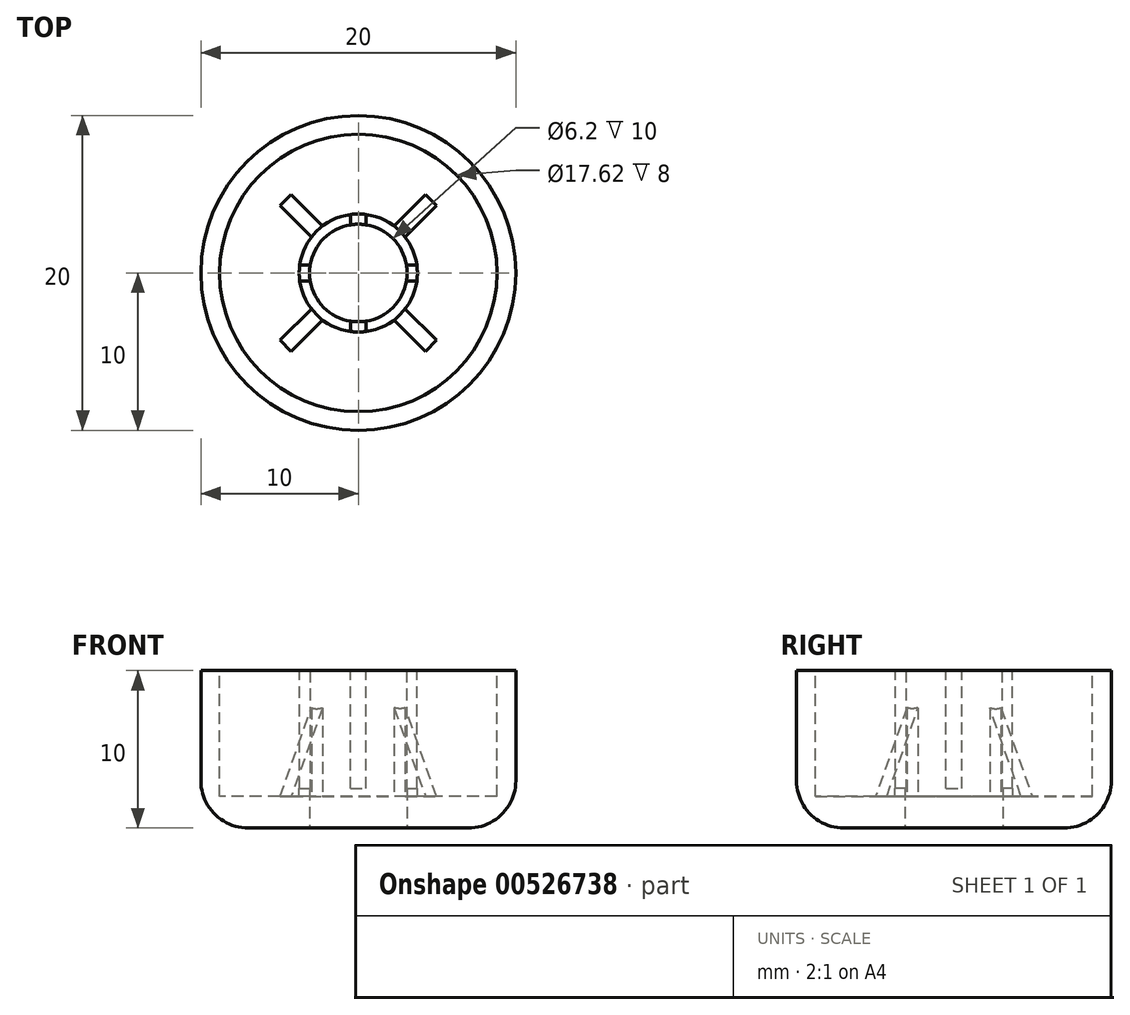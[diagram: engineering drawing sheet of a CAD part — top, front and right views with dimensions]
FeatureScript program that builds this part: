
annotation { "Feature Type Name" : "Feature", "Feature Type Description" : "" }
export const myFeature = defineFeature(function(context is Context, id is Id, definition is map)
    precondition{}
    {
        {
            var Q0;
            Q0=qCreatedBy(makeId("Top.planeOp"),FACE);
            var sketch = newSketch(context, id + "F0", { "sketchPlane" : qUnion([Q0])});
            skCircle(sketch, "E0", {"center": v(0, 0) * mm, "radius": 3.1 * mm});
            skCircle(sketch, "E1", {"center": v(0, 0) * mm, "radius": 10 * mm});
            skSolve(sketch);
        }
        {
            var Q0;
            Q0 = qSketchRegion(id + "F0", true);
            extrude(context, id + "F1", {"entities" : qUnion([Q0]), "depth" : 10 * mm, "offsetDistance" : 25.4 * mm});
        }
        {
            var Q0;
            Q0=makeQuery(id+"F1.opExtrude","CAP_FACE",FACE,{"disambiguationData":[OSD([sQuery(id+"F0.wireOp",EDGE,"E0"),sQuery(id+"F0.wireOp",EDGE,"E1")])],"isStart":false});
            var sketch = newSketch(context, id + "F2", { "sketchPlane" : qUnion([Q0])});
            skCircle(sketch, "E2", {"center": v(0, 0) * mm, "radius": 3.75 * mm});
            skCircle(sketch, "E3", {"center": v(0, 0) * mm, "radius": 8.8 * mm});
            skSolve(sketch);
        }
        {
            var Q0;
            Q0 = qSketchRegion(id + "F2", true);
            extrude(context, id + "F3", {"entities" : qUnion([Q0]), "operationType" : NewBodyOperationType.REMOVE, "oppositeDirection" : true, "depth" : 8 * mm, "offsetDistance" : 25.4 * mm});
        }
        {
            var Q0;
            {var subQ0=sQuery(id+"F0.wireOp",EDGE,"E0");Q0=makeQuery(id+"F3.boolean.opBoolean","SPLIT",FACE,{"disambiguationData":[TD([makeQuery(id+"F1.opExtrude","SWEPT_FACE",FACE,{"disambiguationData":[OSD([subQ0])]})])],"derivedFrom":makeQuery(id+"F1.opExtrude","CAP_FACE",FACE,{"disambiguationData":[OSD([subQ0,sQuery(id+"F0.wireOp",EDGE,"E1")])],"isStart":false})});}
            var sketch = newSketch(context, id + "F4", { "sketchPlane" : qUnion([Q0])});
            skLineSegment(sketch, "E4", {"start": v(-4.82, 0.5) * mm, "end": v(-2.74, 0.5) * mm});
            skLineSegment(sketch, "E5", {"start": v(-2.74, 0.5) * mm, "end": v(-2.74, -0.5) * mm});
            skLineSegment(sketch, "E6", {"start": v(-2.74, -0.5) * mm, "end": v(-4.86, -0.5) * mm});
            skLineSegment(sketch, "E7", {"start": v(-4.86, -0.5) * mm, "end": v(-4.82, 0.5) * mm});
            skPoint(sketch, "E8.start.orphan", {"position": v(0.06, 5.71) * mm});
            skPoint(sketch, "E9.start.orphan", {"position": v(0.06, -3.27) * mm});
            skLineSegment(sketch, "E10", {"start": v(-0.5, 4.69) * mm, "end": v(-0.5, 1.98) * mm});
            skLineSegment(sketch, "E11", {"start": v(-0.5, 1.98) * mm, "end": v(0.5, 1.98) * mm});
            skLineSegment(sketch, "E12", {"start": v(0.5, 1.98) * mm, "end": v(0.5, 4.89) * mm});
            skLineSegment(sketch, "E13", {"start": v(0.5, 4.89) * mm, "end": v(-0.5, 4.89) * mm});
            skLineSegment(sketch, "E14", {"start": v(-0.5, 4.89) * mm, "end": v(-0.5, 4.69) * mm});
            skLineSegment(sketch, "E15.bottom", {"start": v(-0.5, -1.61) * mm, "end": v(0.5, -1.61) * mm});
            skLineSegment(sketch, "E15.top", {"start": v(-0.5, -4.9) * mm, "end": v(0.5, -4.9) * mm});
            skLineSegment(sketch, "E15.left", {"start": v(-0.5, -1.61) * mm, "end": v(-0.5, -4.9) * mm});
            skLineSegment(sketch, "E15.right", {"start": v(0.5, -1.61) * mm, "end": v(0.5, -4.9) * mm});
            skLineSegment(sketch, "E16.bottom", {"start": v(2.33, 0.5) * mm, "end": v(4.84, 0.5) * mm});
            skLineSegment(sketch, "E16.top", {"start": v(2.33, -0.5) * mm, "end": v(4.84, -0.5) * mm});
            skLineSegment(sketch, "E16.left", {"start": v(2.33, 0.5) * mm, "end": v(2.33, -0.5) * mm});
            skLineSegment(sketch, "E16.right", {"start": v(4.84, 0.5) * mm, "end": v(4.84, -0.5) * mm});
            skSolve(sketch);
        }
        {
            var Q0;
            Q0 = qSketchRegion(id + "F4", true);
            extrude(context, id + "F5", {"entities" : qUnion([Q0]), "operationType" : NewBodyOperationType.REMOVE, "oppositeDirection" : true, "depth" : 7.5 * mm, "offsetDistance" : 25.4 * mm});
        }
        {
            var Q0;
            Q0=makeQuery(id+"F1.opExtrude","CAP_EDGE",EDGE,{"disambiguationData":[OSD([sQuery(id+"F0.wireOp",EDGE,"E1")])],"isStart":true});
            fillet(context, id + "F6", {"entities" : qUnion([Q0]), "radius" : 3 * mm, "tangentPropagation" : true, "allowEdgeOverflow" : false});
        }
        {
            var Q0;
            Q0=makeQuery(id+"F3.boolean.opBoolean","COPY",FACE,{"derivedFrom":makeQuery(id+"F3.opExtrude","CAP_FACE",FACE,{"disambiguationData":[OSD([sQuery(id+"F2.wireOp",EDGE,"E2"),sQuery(id+"F2.wireOp",EDGE,"E3")])],"isStart":false})});
            var sketch = newSketch(context, id + "F7", { "sketchPlane" : qUnion([Q0])});
            skLineSegment(sketch, "E17", {"start": v(-2.98, 2.27) * mm, "end": v(-4.98, 4.27) * mm});
            skLineSegment(sketch, "E18", {"start": v(-4.98, 4.27) * mm, "end": v(-4.27, 4.98) * mm});
            skLineSegment(sketch, "E19", {"start": v(-4.27, 4.98) * mm, "end": v(-2.27, 2.98) * mm});
            skLineSegment(sketch, "E20", {"start": v(-2.27, 2.98) * mm, "end": v(-2.98, 2.27) * mm});
            skLineSegment(sketch, "E21.MirrorCS", {"start": v(2.98, 2.27) * mm, "end": v(4.98, 4.27) * mm});
            skLineSegment(sketch, "E22.MirrorCS", {"start": v(4.98, 4.27) * mm, "end": v(4.27, 4.98) * mm});
            skLineSegment(sketch, "E23.MirrorCS", {"start": v(4.27, 4.98) * mm, "end": v(2.27, 2.98) * mm});
            skLineSegment(sketch, "E24.MirrorCS", {"start": v(2.27, 2.98) * mm, "end": v(2.98, 2.27) * mm});
            skLineSegment(sketch, "E25.MirrorCS", {"start": v(-2.98, -2.27) * mm, "end": v(-4.98, -4.27) * mm});
            skLineSegment(sketch, "E26.MirrorCS", {"start": v(-4.98, -4.27) * mm, "end": v(-4.27, -4.98) * mm});
            skLineSegment(sketch, "E27.MirrorCS", {"start": v(-4.27, -4.98) * mm, "end": v(-2.27, -2.98) * mm});
            skLineSegment(sketch, "E28.MirrorCS", {"start": v(2.27, -2.98) * mm, "end": v(2.98, -2.27) * mm});
            skLineSegment(sketch, "E29.MirrorCS", {"start": v(-2.27, -2.98) * mm, "end": v(-2.98, -2.27) * mm});
            skLineSegment(sketch, "E30.MirrorCS", {"start": v(2.98, -2.27) * mm, "end": v(4.98, -4.27) * mm});
            skLineSegment(sketch, "E31.MirrorCS", {"start": v(4.98, -4.27) * mm, "end": v(4.27, -4.98) * mm});
            skLineSegment(sketch, "E32.MirrorCS", {"start": v(4.27, -4.98) * mm, "end": v(2.27, -2.98) * mm});
            skPoint(sketch, "E33.orphan", {"position": v(0, 0) * mm});
            skPoint(sketch, "E34.end.orphan", {"position": v(-5.02, 5.02) * mm});
            skPoint(sketch, "E35.MirrorCS.end.orphan", {"position": v(5.02, 5.02) * mm});
            skSolve(sketch);
        }
        {
            var Q0;
            Q0 = qSketchRegion(id + "F7", true);
            extrude(context, id + "F8", {"entities" : qUnion([Q0]), "operationType" : NewBodyOperationType.ADD, "depth" : 6 * mm, "offsetDistance" : 25.4 * mm});
        }
        {
            var Q0;
            Q0=makeQuery(id+"F8.opExtrude","CAP_EDGE",EDGE,{"disambiguationData":[OSD([sQuery(id+"F7.wireOp",EDGE,"E18")])],"isStart":false});
            var Q1;
            Q1=makeQuery(id+"F8.opExtrude","CAP_EDGE",EDGE,{"disambiguationData":[OSD([sQuery(id+"F7.wireOp",EDGE,"E31.MirrorCS")])],"isStart":false});
            chamfer(context, id + "F9", {"entities" : qUnion([Q0, Q1]), "chamferType" : ChamferType.TWO_OFFSETS, "width1" : 6 * mm, "oppositeDirection" : false, "width2" : 3 * mm, "tangentPropagation" : true});
        }
        {
            var Q0;
            Q0=makeQuery(id+"F8.opExtrude","CAP_EDGE",EDGE,{"disambiguationData":[OSD([sQuery(id+"F7.wireOp",EDGE,"E22.MirrorCS")])],"isStart":false});
            var Q1;
            Q1=makeQuery(id+"F8.opExtrude","CAP_EDGE",EDGE,{"disambiguationData":[OSD([sQuery(id+"F7.wireOp",EDGE,"E26.MirrorCS")])],"isStart":false});
            chamfer(context, id + "F10", {"entities" : qUnion([Q0, Q1]), "chamferType" : ChamferType.TWO_OFFSETS, "width1" : 3 * mm, "oppositeDirection" : false, "width2" : 6 * mm, "tangentPropagation" : true});
        }
    });
